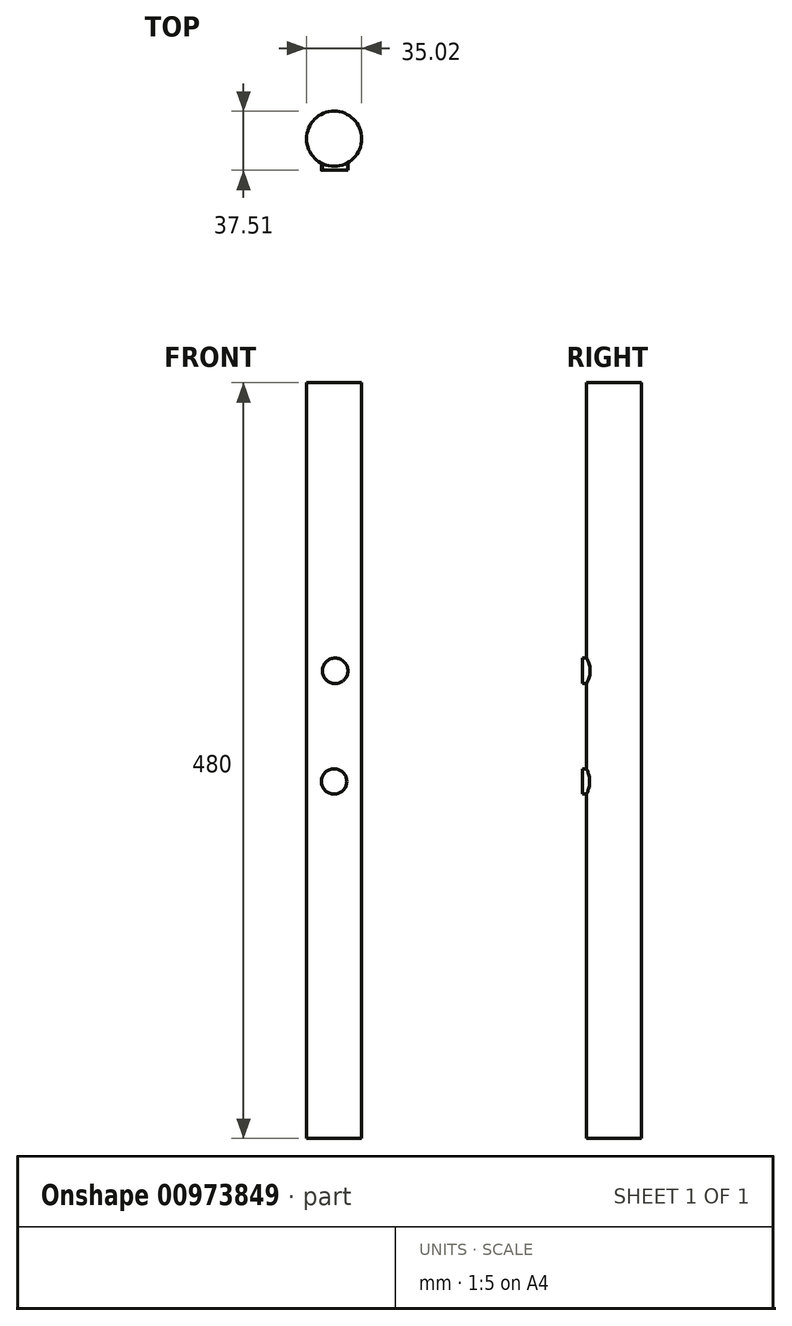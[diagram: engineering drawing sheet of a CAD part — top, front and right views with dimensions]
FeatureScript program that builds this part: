
annotation { "Feature Type Name" : "Feature", "Feature Type Description" : "" }
export const myFeature = defineFeature(function(context is Context, id is Id, definition is map)
    precondition{}
    {
        {
            var Q0;
            Q0=qCreatedBy(makeId("Top.planeOp"),FACE);
            var sketch = newSketch(context, id + "F0", { "sketchPlane" : qUnion([Q0])});
            skCircle(sketch, "E0", {"center": v(0, 0) * mm, "radius": 17.5 * mm});
            skSolve(sketch);
        }
        {
            var Q0;
            Q0 = qSketchRegion(id + "F0", true);
            extrude(context, id + "F1", {"entities" : qUnion([Q0]), "depth" : 480 * mm, "offsetDistance" : 25 * mm});
        }
        {
            var Q0;
            Q0=qCreatedBy(makeId("Front.planeOp"),FACE);
            var sketch = newSketch(context, id + "F2", { "sketchPlane" : qUnion([Q0])});
            skCircle(sketch, "E1", {"center": v(0, 226.75) * mm, "radius": 8.06 * mm});
            skSolve(sketch);
        }
        {
            var Q0;
            Q0 = qSketchRegion(id + "F2", true);
            extrude(context, id + "F3", {"entities" : qUnion([Q0]), "operationType" : NewBodyOperationType.ADD, "depth" : 20 * mm, "offsetDistance" : 25 * mm});
        }
        {
            var Q0;
            Q0=qCreatedBy(makeId("Front.planeOp"),FACE);
            var sketch = newSketch(context, id + "F4", { "sketchPlane" : qUnion([Q0])});
            skCircle(sketch, "E2", {"center": v(0.67, 297.02) * mm, "radius": 8.06 * mm});
            skSolve(sketch);
        }
        {
            var Q0;
            Q0 = qSketchRegion(id + "F4", true);
            extrude(context, id + "F5", {"entities" : qUnion([Q0]), "operationType" : NewBodyOperationType.ADD, "depth" : 20 * mm, "offsetDistance" : 25 * mm});
        }
    });
